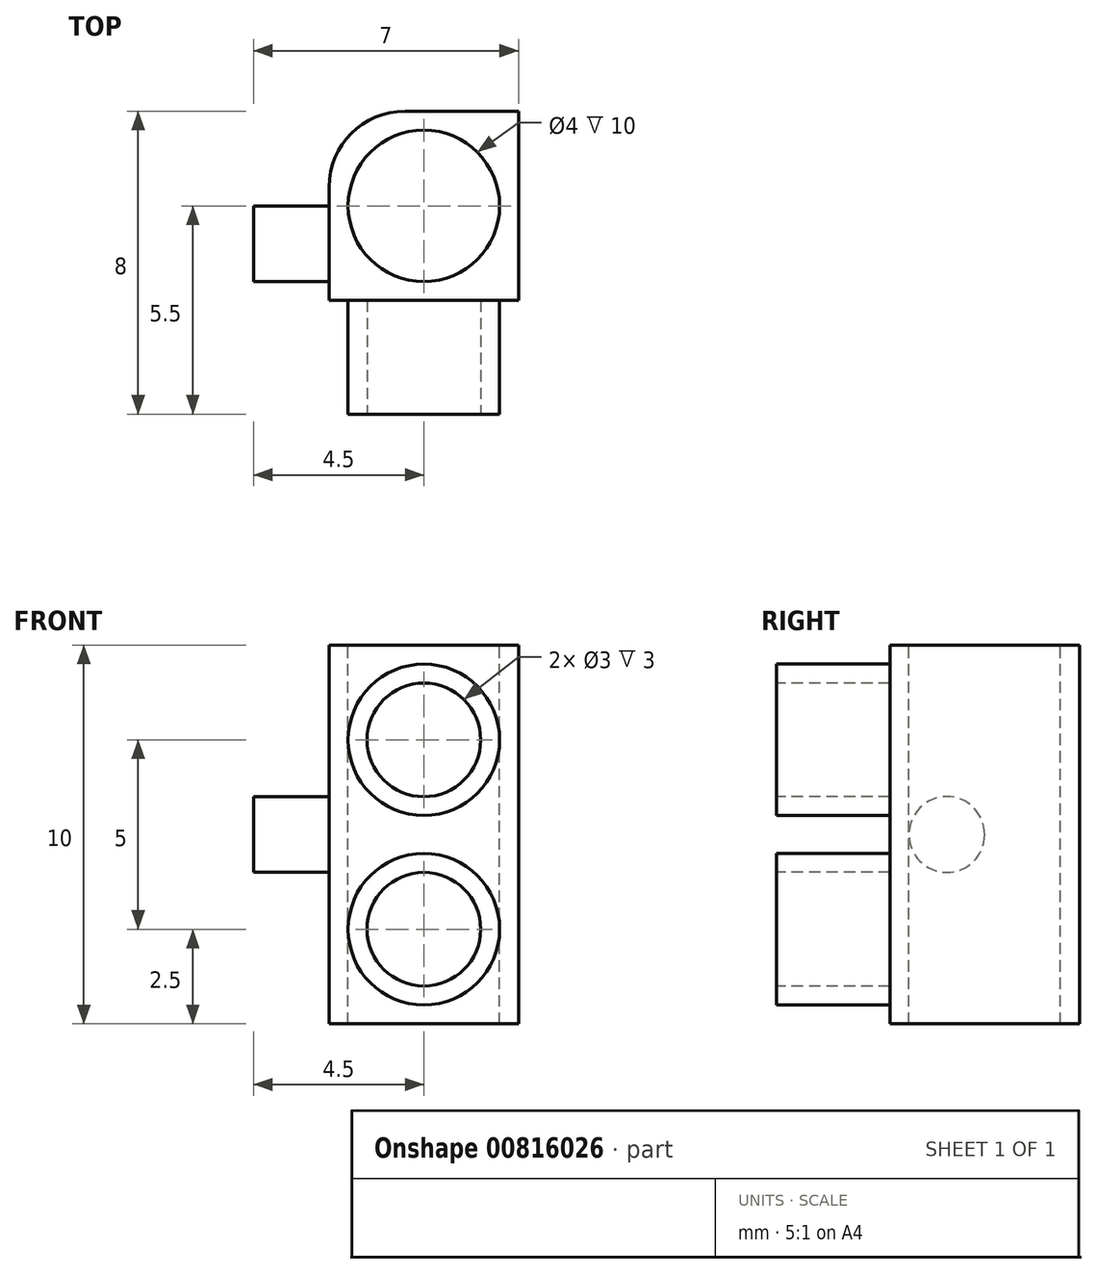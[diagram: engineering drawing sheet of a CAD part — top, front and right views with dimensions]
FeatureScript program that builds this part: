
annotation { "Feature Type Name" : "Feature", "Feature Type Description" : "" }
export const myFeature = defineFeature(function(context is Context, id is Id, definition is map)
    precondition{}
    {
        {
            var Q0;
            Q0=qCreatedBy(makeId("Front.planeOp"),FACE);
            var sketch = newSketch(context, id + "F0", { "sketchPlane" : qUnion([Q0])});
            skLineSegment(sketch, "E0.bottom", {"start": v(-2.5, 5) * mm, "end": v(2.5, 5) * mm});
            skLineSegment(sketch, "E0.top", {"start": v(-2.5, -5) * mm, "end": v(2.5, -5) * mm});
            skLineSegment(sketch, "E0.left", {"start": v(-2.5, 5) * mm, "end": v(-2.5, -5) * mm});
            skLineSegment(sketch, "E0.right", {"start": v(2.5, 5) * mm, "end": v(2.5, -5) * mm});
            skPoint(sketch, "E0.middle", {"position": v(0, 0) * mm});
            skSolve(sketch);
        }
        {
            var Q0;
            Q0=makeQuery(id+"F0.imprint","IMPRINT",FACE,{"disambiguationData":[TD([[makeQuery(id+"F0.imprint","IMPRINT",EDGE,{"derivedFrom":sQuery(id+"F0.wireOp",EDGE,"E0.bottom")}),-1.0]])]});
            extrude(context, id + "F1", {"entities" : qUnion([Q0]), "depth" : 8 * mm, "offsetDistance" : 25 * mm, "symmetric" : true});
        }
        {
            var Q0;
            Q0=makeQuery(id+"F1.opExtrude","CAP_FACE",FACE,{"disambiguationData":[OSD([sQuery(id+"F0.wireOp",EDGE,"E0.bottom"),sQuery(id+"F0.wireOp",EDGE,"E0.top"),sQuery(id+"F0.wireOp",EDGE,"E0.left"),sQuery(id+"F0.wireOp",EDGE,"E0.right")])],"isStart":false});
            var sketch = newSketch(context, id + "F2", { "sketchPlane" : qUnion([Q0])});
            skLineSegment(sketch, "E1", {"start": v(-2.5, 5) * mm, "end": v(2.5, 5) * mm});
            skLineSegment(sketch, "E2", {"start": v(2.5, 5) * mm, "end": v(2.5, 1) * mm});
            skLineSegment(sketch, "E3", {"start": v(2.5, 1) * mm, "end": v(4.5, 1) * mm});
            skLineSegment(sketch, "E4", {"start": v(4.5, 1) * mm, "end": v(4.5, 5) * mm});
            skLineSegment(sketch, "E5", {"start": v(4.5, 5) * mm, "end": v(9.5, 5) * mm});
            skLineSegment(sketch, "E6", {"start": v(9.5, 5) * mm, "end": v(9.5, 1) * mm});
            skLineSegment(sketch, "E7", {"start": v(9.5, 1) * mm, "end": v(11.5, 1) * mm});
            skLineSegment(sketch, "E8", {"start": v(11.5, 1) * mm, "end": v(11.5, 5) * mm});
            skLineSegment(sketch, "E9", {"start": v(11.5, 5) * mm, "end": v(16.5, 5) * mm});
            skLineSegment(sketch, "E10", {"start": v(16.5, 5) * mm, "end": v(16.5, 1) * mm});
            skLineSegment(sketch, "E11", {"start": v(16.5, 1) * mm, "end": v(18.5, 1) * mm});
            skLineSegment(sketch, "E12", {"start": v(18.5, 1) * mm, "end": v(18.5, 5) * mm});
            skLineSegment(sketch, "E13", {"start": v(2.5, 5) * mm, "end": v(18.5, 5) * mm});
            skLineSegment(sketch, "E14", {"start": v(2.5, 5) * mm, "end": v(2.5, -5) * mm});
            skLineSegment(sketch, "E15", {"start": v(18.5, -5) * mm, "end": v(2.5, -5) * mm});
            skLineSegment(sketch, "E16", {"start": v(18.5, -5) * mm, "end": v(18.5, -1) * mm});
            skLineSegment(sketch, "E17", {"start": v(18.5, -1) * mm, "end": v(16.5, -1) * mm});
            skLineSegment(sketch, "E18", {"start": v(16.5, -1) * mm, "end": v(16.5, -5) * mm});
            skLineSegment(sketch, "E19", {"start": v(16.5, -5) * mm, "end": v(11.5, -5) * mm});
            skLineSegment(sketch, "E20", {"start": v(11.5, -5) * mm, "end": v(11.5, -1) * mm});
            skLineSegment(sketch, "E21", {"start": v(11.5, -1) * mm, "end": v(9.5, -1) * mm});
            skLineSegment(sketch, "E22", {"start": v(9.5, -1) * mm, "end": v(9.5, -5) * mm});
            skLineSegment(sketch, "E23", {"start": v(9.5, -5) * mm, "end": v(4.5, -5) * mm});
            skLineSegment(sketch, "E24", {"start": v(4.5, -5) * mm, "end": v(4.5, -1) * mm});
            skLineSegment(sketch, "E25", {"start": v(4.5, -1) * mm, "end": v(2.5, -1) * mm});
            skLineSegment(sketch, "E26", {"start": v(2.5, -1) * mm, "end": v(2.5, -5) * mm});
            skLineSegment(sketch, "E27", {"start": v(2.5, -5) * mm, "end": v(-2.5, -5) * mm});
            skLineSegment(sketch, "E28", {"start": v(-2.5, -5) * mm, "end": v(-2.5, 5) * mm});
            skSolve(sketch);
        }
        {
            var Q0;
            {var subQ0=sQuery(id+"F2.wireOp",EDGE,"E2");Q0=makeQuery(id+"F2.imprint","IMPRINT",FACE,{"disambiguationData":[TD([[makeQuery(id+"F2.imprint","IMPRINT",EDGE,{"derivedFrom":subQ0}),1.0]])]});}
            var Q1;
            {var subQ0=sQuery(id+"F2.wireOp",EDGE,"E6");Q1=makeQuery(id+"F2.imprint","IMPRINT",FACE,{"disambiguationData":[TD([[makeQuery(id+"F2.imprint","IMPRINT",EDGE,{"derivedFrom":subQ0}),1.0]])]});}
            var Q2;
            {var subQ0=sQuery(id+"F2.wireOp",EDGE,"E10");Q2=makeQuery(id+"F2.imprint","IMPRINT",FACE,{"disambiguationData":[TD([[makeQuery(id+"F2.imprint","IMPRINT",EDGE,{"derivedFrom":subQ0}),1.0]])]});}
            var Q3;
            {var subQ0=sQuery(id+"F2.wireOp",EDGE,"E16");Q3=makeQuery(id+"F2.imprint","IMPRINT",FACE,{"disambiguationData":[TD([[makeQuery(id+"F2.imprint","IMPRINT",EDGE,{"derivedFrom":subQ0}),1.0]])]});}
            var Q4;
            {var subQ0=sQuery(id+"F2.wireOp",EDGE,"E20");Q4=makeQuery(id+"F2.imprint","IMPRINT",FACE,{"disambiguationData":[TD([[makeQuery(id+"F2.imprint","IMPRINT",EDGE,{"derivedFrom":subQ0}),1.0]])]});}
            var Q5;
            {var subQ0=sQuery(id+"F2.wireOp",EDGE,"E24");Q5=makeQuery(id+"F2.imprint","IMPRINT",FACE,{"disambiguationData":[TD([[makeQuery(id+"F2.imprint","IMPRINT",EDGE,{"derivedFrom":subQ0}),1.0]])]});}
            extrude(context, id + "F3", {"entities" : qUnion([Q0, Q1, Q2, Q3, Q4, Q5]), "operationType" : NewBodyOperationType.REMOVE, "oppositeDirection" : true, "depth" : 25 * mm, "offsetDistance" : 25 * mm});
        }
        {
            var Q0;
            Q0=makeQuery(id+"F1.opExtrude","CAP_EDGE",EDGE,{"disambiguationData":[OSD([sQuery(id+"F0.wireOp",EDGE,"E0.left")])],"isStart":true});
            var Q1;
            {var subQ0=makeQuery(id+"F1.opExtrude","CAP_FACE",FACE,{"disambiguationData":[OSD([sQuery(id+"F0.wireOp",EDGE,"E0.bottom"),sQuery(id+"F0.wireOp",EDGE,"E0.top"),sQuery(id+"F0.wireOp",EDGE,"E0.left"),sQuery(id+"F0.wireOp",EDGE,"E0.right")])],"isStart":true});Q1=makeQuery(id+"FKoRw4XPYFI4gUD_1.boolean.opBoolean","MERGE",EDGE,{"derivedFrom":[makeQuery(id+"F3.boolean.opBoolean","INTERSECT",EDGE,{"derivedFrom":[subQ0,makeQuery(id+"F3.opExtrude","SWEPT_FACE",FACE,{"disambiguationData":[OSD([sQuery(id+"F2.wireOp",EDGE,"E2")])]})]}),makeQuery(id+"F3.boolean.opBoolean","INTERSECT",EDGE,{"derivedFrom":[subQ0,makeQuery(id+"F3.opExtrude","SWEPT_FACE",FACE,{"disambiguationData":[OSD([sQuery(id+"F2.wireOp",EDGE,"E26")])]})]}),makeQuery(id+"FKoRw4XPYFI4gUD_1.opExtrude","SWEPT_EDGE",EDGE,{"disambiguationData":[OSD([sQuery(id+"FIU8s27CPLg3rdI_1.wireOp",EDGE,"eRZErHEs-PkYd-TQZp-d9e6-CNfVVQBMXokK.bottom"),sQuery(id+"FIU8s27CPLg3rdI_1.wireOp",EDGE,"eRZErHEs-PkYd-TQZp-d9e6-CNfVVQBMXokK.right")])]})]});}
            var Q2;
            {var subQ0=makeQuery(id+"F1.opExtrude","CAP_FACE",FACE,{"disambiguationData":[OSD([sQuery(id+"F0.wireOp",EDGE,"E0.bottom"),sQuery(id+"F0.wireOp",EDGE,"E0.top"),sQuery(id+"F0.wireOp",EDGE,"E0.left"),sQuery(id+"F0.wireOp",EDGE,"E0.right")])],"isStart":true});Q2=makeQuery(id+"FKoRw4XPYFI4gUD_1.boolean.opBoolean","MERGE",EDGE,{"derivedFrom":[makeQuery(id+"F3.boolean.opBoolean","INTERSECT",EDGE,{"derivedFrom":[subQ0,makeQuery(id+"F3.opExtrude","SWEPT_FACE",FACE,{"disambiguationData":[OSD([sQuery(id+"F2.wireOp",EDGE,"E4")])]})]}),makeQuery(id+"F3.boolean.opBoolean","INTERSECT",EDGE,{"derivedFrom":[subQ0,makeQuery(id+"F3.opExtrude","SWEPT_FACE",FACE,{"disambiguationData":[OSD([sQuery(id+"F2.wireOp",EDGE,"E24")])]})]}),makeQuery(id+"FKoRw4XPYFI4gUD_1.opExtrude","SWEPT_EDGE",EDGE,{"disambiguationData":[OSD([sQuery(id+"FIU8s27CPLg3rdI_1.wireOp",EDGE,"eRZErHEs-PkYd-TQZp-d9e6-CNfVVQBMXokK.bottom"),sQuery(id+"FIU8s27CPLg3rdI_1.wireOp",EDGE,"eRZErHEs-PkYd-TQZp-d9e6-CNfVVQBMXokK.left")])]})]});}
            var Q3;
            {var subQ0=makeQuery(id+"F1.opExtrude","CAP_FACE",FACE,{"disambiguationData":[OSD([sQuery(id+"F0.wireOp",EDGE,"E0.bottom"),sQuery(id+"F0.wireOp",EDGE,"E0.top"),sQuery(id+"F0.wireOp",EDGE,"E0.left"),sQuery(id+"F0.wireOp",EDGE,"E0.right")])],"isStart":true});Q3=makeQuery(id+"FKoRw4XPYFI4gUD_1.boolean.opBoolean","MERGE",EDGE,{"derivedFrom":[makeQuery(id+"F3.boolean.opBoolean","INTERSECT",EDGE,{"derivedFrom":[subQ0,makeQuery(id+"F3.opExtrude","SWEPT_FACE",FACE,{"disambiguationData":[OSD([sQuery(id+"F2.wireOp",EDGE,"E6")])]})]}),makeQuery(id+"F3.boolean.opBoolean","INTERSECT",EDGE,{"derivedFrom":[subQ0,makeQuery(id+"F3.opExtrude","SWEPT_FACE",FACE,{"disambiguationData":[OSD([sQuery(id+"F2.wireOp",EDGE,"E22")])]})]}),makeQuery(id+"FKoRw4XPYFI4gUD_1.opExtrude","SWEPT_EDGE",EDGE,{"disambiguationData":[OSD([sQuery(id+"Fn3xYcwA6SLb2X5_1.wireOp",EDGE,"7jzVOehx-xfHW-CI5p-Tc8N-ebZ9P9cge40l.bottom"),sQuery(id+"Fn3xYcwA6SLb2X5_1.wireOp",EDGE,"7jzVOehx-xfHW-CI5p-Tc8N-ebZ9P9cge40l.left")])]})]});}
            var Q4;
            {var subQ0=makeQuery(id+"F1.opExtrude","CAP_FACE",FACE,{"disambiguationData":[OSD([sQuery(id+"F0.wireOp",EDGE,"E0.bottom"),sQuery(id+"F0.wireOp",EDGE,"E0.top"),sQuery(id+"F0.wireOp",EDGE,"E0.left"),sQuery(id+"F0.wireOp",EDGE,"E0.right")])],"isStart":true});Q4=makeQuery(id+"FKoRw4XPYFI4gUD_1.boolean.opBoolean","MERGE",EDGE,{"derivedFrom":[makeQuery(id+"F3.boolean.opBoolean","INTERSECT",EDGE,{"derivedFrom":[subQ0,makeQuery(id+"F3.opExtrude","SWEPT_FACE",FACE,{"disambiguationData":[OSD([sQuery(id+"F2.wireOp",EDGE,"E8")])]})]}),makeQuery(id+"F3.boolean.opBoolean","INTERSECT",EDGE,{"derivedFrom":[subQ0,makeQuery(id+"F3.opExtrude","SWEPT_FACE",FACE,{"disambiguationData":[OSD([sQuery(id+"F2.wireOp",EDGE,"E20")])]})]}),makeQuery(id+"FKoRw4XPYFI4gUD_1.opExtrude","SWEPT_EDGE",EDGE,{"disambiguationData":[OSD([sQuery(id+"Fn3xYcwA6SLb2X5_1.wireOp",EDGE,"7jzVOehx-xfHW-CI5p-Tc8N-ebZ9P9cge40l.bottom"),sQuery(id+"Fn3xYcwA6SLb2X5_1.wireOp",EDGE,"7jzVOehx-xfHW-CI5p-Tc8N-ebZ9P9cge40l.right")])]})]});}
            var Q5;
            {var subQ0=makeQuery(id+"F1.opExtrude","CAP_FACE",FACE,{"disambiguationData":[OSD([sQuery(id+"F0.wireOp",EDGE,"E0.bottom"),sQuery(id+"F0.wireOp",EDGE,"E0.top"),sQuery(id+"F0.wireOp",EDGE,"E0.left"),sQuery(id+"F0.wireOp",EDGE,"E0.right")])],"isStart":true});Q5=makeQuery(id+"FKoRw4XPYFI4gUD_1.boolean.opBoolean","MERGE",EDGE,{"derivedFrom":[makeQuery(id+"F3.boolean.opBoolean","INTERSECT",EDGE,{"derivedFrom":[subQ0,makeQuery(id+"F3.opExtrude","SWEPT_FACE",FACE,{"disambiguationData":[OSD([sQuery(id+"F2.wireOp",EDGE,"E10")])]})]}),makeQuery(id+"F3.boolean.opBoolean","INTERSECT",EDGE,{"derivedFrom":[subQ0,makeQuery(id+"F3.opExtrude","SWEPT_FACE",FACE,{"disambiguationData":[OSD([sQuery(id+"F2.wireOp",EDGE,"E18")])]})]}),makeQuery(id+"FKoRw4XPYFI4gUD_1.opExtrude","SWEPT_EDGE",EDGE,{"disambiguationData":[OSD([sQuery(id+"F23fy8IZEQtN0Ie_1.wireOp",EDGE,"QXJKDjhw-bfeQ-h6R5-7f2p-KXr9aezmBCs4.bottom"),sQuery(id+"F23fy8IZEQtN0Ie_1.wireOp",EDGE,"QXJKDjhw-bfeQ-h6R5-7f2p-KXr9aezmBCs4.right")])]})]});}
            var Q6;
            {var subQ0=makeQuery(id+"F1.opExtrude","CAP_FACE",FACE,{"disambiguationData":[OSD([sQuery(id+"F0.wireOp",EDGE,"E0.bottom"),sQuery(id+"F0.wireOp",EDGE,"E0.top"),sQuery(id+"F0.wireOp",EDGE,"E0.left"),sQuery(id+"F0.wireOp",EDGE,"E0.right")])],"isStart":true});Q6=makeQuery(id+"FKoRw4XPYFI4gUD_1.boolean.opBoolean","MERGE",EDGE,{"derivedFrom":[makeQuery(id+"F3.boolean.opBoolean","INTERSECT",EDGE,{"derivedFrom":[subQ0,makeQuery(id+"F3.opExtrude","SWEPT_FACE",FACE,{"disambiguationData":[OSD([sQuery(id+"F2.wireOp",EDGE,"E12")])]})]}),makeQuery(id+"F3.boolean.opBoolean","INTERSECT",EDGE,{"derivedFrom":[subQ0,makeQuery(id+"F3.opExtrude","SWEPT_FACE",FACE,{"disambiguationData":[OSD([sQuery(id+"F2.wireOp",EDGE,"E16")])]})]}),makeQuery(id+"FKoRw4XPYFI4gUD_1.opExtrude","SWEPT_EDGE",EDGE,{"disambiguationData":[OSD([sQuery(id+"F23fy8IZEQtN0Ie_1.wireOp",EDGE,"QXJKDjhw-bfeQ-h6R5-7f2p-KXr9aezmBCs4.bottom"),sQuery(id+"F23fy8IZEQtN0Ie_1.wireOp",EDGE,"QXJKDjhw-bfeQ-h6R5-7f2p-KXr9aezmBCs4.left")])]})]});}
            var Q7;
            Q7=makeQuery(id+"F1.opExtrude","CAP_EDGE",EDGE,{"disambiguationData":[OSD([sQuery(id+"F0.wireOp",EDGE,"E0.right")])],"isStart":true});
            fillet(context, id + "F4", {"entities" : qUnion([Q0, Q1, Q2, Q3, Q4, Q5, Q6, Q7]), "radius" : 2 * mm, "tangentPropagation" : true, "allowEdgeOverflow" : false});
        }
        {
            var Q0;
            {var subQ3=sQuery(id+"F0.wireOp",EDGE,"E0.bottom");Q0=makeQuery(id+"F3.boolean.opBoolean","SPLIT",FACE,{"disambiguationData":[TD([makeQuery(id+"F3.opExtrude","SWEPT_FACE",FACE,{"disambiguationData":[OSD([sQuery(id+"F2.wireOp",EDGE,"E8")])]})])],"derivedFrom":makeQuery(id+"F1.opExtrude","SWEPT_FACE",FACE,{"disambiguationData":[OSD([subQ3])]})});}
            var sketch = newSketch(context, id + "F5", { "sketchPlane" : qUnion([Q0])});
            skLineSegment(sketch, "E29", {"start": v(0, 4) * mm, "end": v(0, 1.5) * mm});
            skCircle(sketch, "E30", {"center": v(0, 1.5) * mm, "radius": 2 * mm});
            skSolve(sketch);
        }
        {
            var Q0;
            {var subQ0=sQuery(id+"F0.wireOp",EDGE,"E0.left");var subQ1=sQuery(id+"F0.wireOp",EDGE,"E0.top");var subQ2=sQuery(id+"F0.wireOp",EDGE,"E0.bottom");Q0=makeQuery(id+"FKoRw4XPYFI4gUD_1.boolean.opBoolean","SPLIT",FACE,{"disambiguationData":[TD([makeQuery(id+"F1.opExtrude","SWEPT_FACE",FACE,{"disambiguationData":[OSD([subQ0])]})])],"derivedFrom":makeQuery(id+"F1.opExtrude","CAP_FACE",FACE,{"disambiguationData":[OSD([subQ2,subQ1,subQ0,sQuery(id+"F0.wireOp",EDGE,"E0.right")])],"isStart":false})});}
            var sketch = newSketch(context, id + "F6", { "sketchPlane" : qUnion([Q0])});
            skLineSegment(sketch, "E31", {"start": v(0, 5) * mm, "end": v(0, 2.5) * mm});
            skLineSegment(sketch, "E32", {"start": v(0, 2.5) * mm, "end": v(0, -2.5) * mm});
            skCircle(sketch, "E33", {"center": v(0, 2.5) * mm, "radius": 1.5 * mm});
            skCircle(sketch, "E34", {"center": v(0, -2.5) * mm, "radius": 1.5 * mm});
            skCircle(sketch, "E35.0", {"center": v(0, 2.5) * mm, "radius": 2 * mm});
            skCircle(sketch, "E36.0", {"center": v(0, -2.5) * mm, "radius": 2 * mm});
            skSolve(sketch);
        }
        {
            var Q0;
            Q0=makeQuery(id+"FF79RMgpESgGzJH_1.imprint","IMPRINT",FACE,{"disambiguationData":[TD([[makeQuery(id+"FF79RMgpESgGzJH_1.imprint","IMPRINT",EDGE,{"derivedFrom":sQuery(id+"FF79RMgpESgGzJH_1.wireOp",EDGE,"d59de9a4-0b82-45a7-9f5f-c8198fa25f41.0")}),-1.0]])]});
            var Q1;
            Q1=makeQuery(id+"FHZJ6tBzDyFADrw_1.imprint","IMPRINT",FACE,{"disambiguationData":[TD([[makeQuery(id+"FHZJ6tBzDyFADrw_1.imprint","IMPRINT",EDGE,{"derivedFrom":sQuery(id+"FHZJ6tBzDyFADrw_1.wireOp",EDGE,"d6111bf3-017d-4c33-bba5-28bb25ad6c81.0")}),-1.0]])]});
            var Q2;
            Q2=makeQuery(id+"Fr8Fn9fYbl4uaWv_1.imprint","IMPRINT",FACE,{"disambiguationData":[TD([[makeQuery(id+"Fr8Fn9fYbl4uaWv_1.imprint","IMPRINT",EDGE,{"derivedFrom":sQuery(id+"Fr8Fn9fYbl4uaWv_1.wireOp",EDGE,"f0623755-3455-4916-b392-23906fbf6834.0")}),-1.0]])]});
            var Q3;
            Q3=makeQuery(id+"F6.imprint","IMPRINT",FACE,{"disambiguationData":[TD([[makeQuery(id+"F6.imprint","IMPRINT",EDGE,{"derivedFrom":sQuery(id+"F6.wireOp",EDGE,"E36.0")}),-1.0]])]});
            var Q4;
            {var subQ0=sQuery(id+"FF79RMgpESgGzJH_1.wireOp",EDGE,"22768ae8-f2dc-462c-b275-2ca9c2483a92");var subQ1=sQuery(id+"FF79RMgpESgGzJH_1.wireOp",EDGE,"0d321b8d-d392-40c1-a30a-78379565c0a7");var subQ2=makeQuery(id+"FF79RMgpESgGzJH_1.imprint","INTERSECT",VERTEX,{"derivedFrom":[subQ1,subQ0]});Q4=makeQuery(id+"FF79RMgpESgGzJH_1.imprint","IMPRINT",FACE,{"disambiguationData":[TD([[makeQuery(id+"FF79RMgpESgGzJH_1.imprint","IMPRINT",EDGE,{"disambiguationData":[TD([[subQ2,1.0]])],"derivedFrom":subQ1}),1.0]])]});}
            var Q5;
            {var subQ0=sQuery(id+"FF79RMgpESgGzJH_1.wireOp",EDGE,"22768ae8-f2dc-462c-b275-2ca9c2483a92");var subQ1=sQuery(id+"FF79RMgpESgGzJH_1.wireOp",EDGE,"0d321b8d-d392-40c1-a30a-78379565c0a7");var subQ2=makeQuery(id+"FF79RMgpESgGzJH_1.imprint","INTERSECT",VERTEX,{"derivedFrom":[subQ1,subQ0]});Q5=makeQuery(id+"FF79RMgpESgGzJH_1.imprint","IMPRINT",FACE,{"disambiguationData":[TD([[makeQuery(id+"FF79RMgpESgGzJH_1.imprint","IMPRINT",EDGE,{"disambiguationData":[TD([[subQ2,1.0]])],"derivedFrom":subQ1}),-1.0]])]});}
            var Q6;
            Q6=makeQuery(id+"FF79RMgpESgGzJH_1.imprint","IMPRINT",FACE,{"disambiguationData":[TD([[makeQuery(id+"FF79RMgpESgGzJH_1.imprint","IMPRINT",EDGE,{"derivedFrom":sQuery(id+"FF79RMgpESgGzJH_1.wireOp",EDGE,"4bb3fbdd-c27a-4cf6-9176-be4444b59b2a")}),1.0]])]});
            var Q7;
            Q7=makeQuery(id+"FHZJ6tBzDyFADrw_1.imprint","IMPRINT",FACE,{"disambiguationData":[TD([[makeQuery(id+"FHZJ6tBzDyFADrw_1.imprint","IMPRINT",EDGE,{"derivedFrom":sQuery(id+"FHZJ6tBzDyFADrw_1.wireOp",EDGE,"3c6ff1fd-0c0a-4439-909a-ac74c9ebc3af")}),1.0]])]});
            var Q8;
            Q8=makeQuery(id+"Fr8Fn9fYbl4uaWv_1.imprint","IMPRINT",FACE,{"disambiguationData":[TD([[makeQuery(id+"Fr8Fn9fYbl4uaWv_1.imprint","IMPRINT",EDGE,{"derivedFrom":sQuery(id+"Fr8Fn9fYbl4uaWv_1.wireOp",EDGE,"720b024b-7175-4fc4-b0d2-a65c40be6c53")}),1.0]])]});
            var Q9;
            Q9=makeQuery(id+"F6.imprint","IMPRINT",FACE,{"disambiguationData":[TD([[makeQuery(id+"F6.imprint","IMPRINT",EDGE,{"derivedFrom":sQuery(id+"F6.wireOp",EDGE,"E34")}),1.0]])]});
            var Q10;
            {var subQ0=sQuery(id+"F6.wireOp",EDGE,"E32");var subQ1=sQuery(id+"F6.wireOp",EDGE,"E31");var subQ2=makeQuery(id+"F6.imprint","INTERSECT",VERTEX,{"derivedFrom":[subQ1,subQ0]});Q10=makeQuery(id+"F6.imprint","IMPRINT",FACE,{"disambiguationData":[TD([[makeQuery(id+"F6.imprint","IMPRINT",EDGE,{"disambiguationData":[TD([[subQ2,1.0]])],"derivedFrom":subQ1}),-1.0]])]});}
            var Q11;
            {var subQ0=sQuery(id+"F6.wireOp",EDGE,"E32");var subQ1=sQuery(id+"F6.wireOp",EDGE,"E31");var subQ2=makeQuery(id+"F6.imprint","INTERSECT",VERTEX,{"derivedFrom":[subQ1,subQ0]});Q11=makeQuery(id+"F6.imprint","IMPRINT",FACE,{"disambiguationData":[TD([[makeQuery(id+"F6.imprint","IMPRINT",EDGE,{"disambiguationData":[TD([[subQ2,1.0]])],"derivedFrom":subQ1}),1.0]])]});}
            var Q12;
            {var subQ0=sQuery(id+"Fr8Fn9fYbl4uaWv_1.wireOp",EDGE,"093e1ef4-a5bb-42be-9e3f-fef99c6f306d");var subQ1=sQuery(id+"Fr8Fn9fYbl4uaWv_1.wireOp",EDGE,"f2b93933-093b-422e-9195-ae5838cce988");var subQ2=makeQuery(id+"Fr8Fn9fYbl4uaWv_1.imprint","INTERSECT",VERTEX,{"derivedFrom":[subQ1,subQ0]});Q12=makeQuery(id+"Fr8Fn9fYbl4uaWv_1.imprint","IMPRINT",FACE,{"disambiguationData":[TD([[makeQuery(id+"Fr8Fn9fYbl4uaWv_1.imprint","IMPRINT",EDGE,{"disambiguationData":[TD([[subQ2,1.0]])],"derivedFrom":subQ1}),-1.0]])]});}
            var Q13;
            {var subQ0=sQuery(id+"Fr8Fn9fYbl4uaWv_1.wireOp",EDGE,"093e1ef4-a5bb-42be-9e3f-fef99c6f306d");var subQ1=sQuery(id+"Fr8Fn9fYbl4uaWv_1.wireOp",EDGE,"f2b93933-093b-422e-9195-ae5838cce988");var subQ2=makeQuery(id+"Fr8Fn9fYbl4uaWv_1.imprint","INTERSECT",VERTEX,{"derivedFrom":[subQ1,subQ0]});Q13=makeQuery(id+"Fr8Fn9fYbl4uaWv_1.imprint","IMPRINT",FACE,{"disambiguationData":[TD([[makeQuery(id+"Fr8Fn9fYbl4uaWv_1.imprint","IMPRINT",EDGE,{"disambiguationData":[TD([[subQ2,1.0]])],"derivedFrom":subQ1}),1.0]])]});}
            var Q14;
            {var subQ0=sQuery(id+"FHZJ6tBzDyFADrw_1.wireOp",EDGE,"27f9dff4-cfe8-4951-bbd8-38729033b4b7");var subQ1=sQuery(id+"FHZJ6tBzDyFADrw_1.wireOp",EDGE,"0b4097b1-70a0-4990-b135-3346e9ae815c");var subQ2=makeQuery(id+"FHZJ6tBzDyFADrw_1.imprint","INTERSECT",VERTEX,{"derivedFrom":[subQ1,subQ0]});Q14=makeQuery(id+"FHZJ6tBzDyFADrw_1.imprint","IMPRINT",FACE,{"disambiguationData":[TD([[makeQuery(id+"FHZJ6tBzDyFADrw_1.imprint","IMPRINT",EDGE,{"disambiguationData":[TD([[subQ2,1.0]])],"derivedFrom":subQ1}),-1.0]])]});}
            var Q15;
            {var subQ0=sQuery(id+"FHZJ6tBzDyFADrw_1.wireOp",EDGE,"27f9dff4-cfe8-4951-bbd8-38729033b4b7");var subQ1=sQuery(id+"FHZJ6tBzDyFADrw_1.wireOp",EDGE,"0b4097b1-70a0-4990-b135-3346e9ae815c");var subQ2=makeQuery(id+"FHZJ6tBzDyFADrw_1.imprint","INTERSECT",VERTEX,{"derivedFrom":[subQ1,subQ0]});Q15=makeQuery(id+"FHZJ6tBzDyFADrw_1.imprint","IMPRINT",FACE,{"disambiguationData":[TD([[makeQuery(id+"FHZJ6tBzDyFADrw_1.imprint","IMPRINT",EDGE,{"disambiguationData":[TD([[subQ2,1.0]])],"derivedFrom":subQ1}),1.0]])]});}
            extrude(context, id + "F7", {"entities" : qUnion([Q0, Q1, Q2, Q3, Q4, Q5, Q6, Q7, Q8, Q9, Q10, Q11, Q12, Q13, Q14, Q15]), "operationType" : NewBodyOperationType.REMOVE, "oppositeDirection" : true, "depth" : 3 * mm, "offsetDistance" : 25 * mm});
        }
        {
            var Q0;
            Q0=makeQuery(id+"F5.imprint","IMPRINT",FACE,{"disambiguationData":[TD([[makeQuery(id+"F5.imprint","IMPRINT",EDGE,{"derivedFrom":sQuery(id+"F5.wireOp",EDGE,"E30")}),1.0]])]});
            extrude(context, id + "F8", {"entities" : qUnion([Q0]), "operationType" : NewBodyOperationType.REMOVE, "oppositeDirection" : true, "depth" : 25 * mm, "offsetDistance" : 25 * mm});
        }
        {
            var Q0;
            Q0=makeQuery(id+"F1.opExtrude","SWEPT_FACE",FACE,{"disambiguationData":[OSD([sQuery(id+"F0.wireOp",EDGE,"E0.left")])]});
            var sketch = newSketch(context, id + "F9", { "sketchPlane" : qUnion([Q0])});
            skPoint(sketch, "E37", {"position": v(-0.5, 0) * mm});
            skCircle(sketch, "E38", {"center": v(-0.5, 0) * mm, "radius": 1 * mm});
            skSolve(sketch);
        }
        {
            var Q0;
            Q0=makeQuery(id+"F9.imprint","IMPRINT",FACE,{"disambiguationData":[TD([[makeQuery(id+"F9.imprint","IMPRINT",EDGE,{"derivedFrom":sQuery(id+"F9.wireOp",EDGE,"E38")}),1.0]])]});
            extrude(context, id + "F10", {"entities" : qUnion([Q0]), "operationType" : NewBodyOperationType.ADD, "depth" : 2 * mm, "offsetDistance" : 25 * mm});
        }
    });
